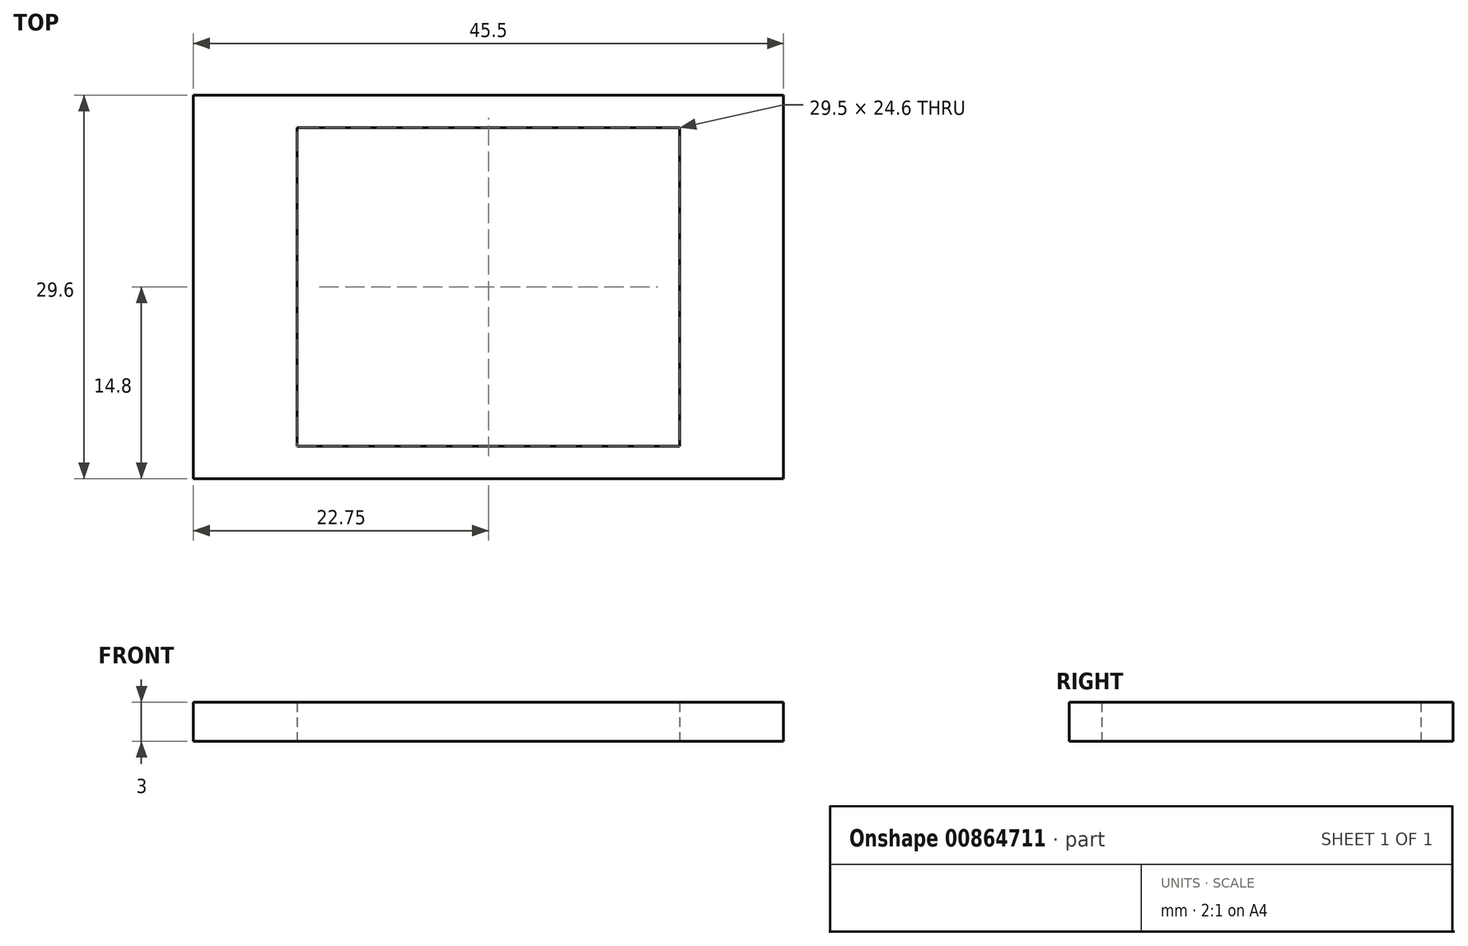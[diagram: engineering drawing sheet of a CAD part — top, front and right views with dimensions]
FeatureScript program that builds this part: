
annotation { "Feature Type Name" : "Feature", "Feature Type Description" : "" }
export const myFeature = defineFeature(function(context is Context, id is Id, definition is map)
    precondition{}
    {
        {
            var Q0;
            Q0=qCreatedBy(makeId("Top.planeOp"),FACE);
            var sketch = newSketch(context, id + "F0", { "sketchPlane" : qUnion([Q0])});
            skLineSegment(sketch, "E0.bottom", {"start": v(0, 0) * mm, "end": v(29.5, 0) * mm});
            skLineSegment(sketch, "E0.top", {"start": v(0, 24.6) * mm, "end": v(29.5, 24.6) * mm});
            skLineSegment(sketch, "E0.left", {"start": v(0, 0) * mm, "end": v(0, 24.6) * mm});
            skLineSegment(sketch, "E0.right", {"start": v(29.5, 0) * mm, "end": v(29.5, 24.6) * mm});
            skLineSegment(sketch, "E1.bottom", {"start": v(-8, 27.1) * mm, "end": v(37.5, 27.1) * mm});
            skLineSegment(sketch, "E1.top", {"start": v(-8, -2.5) * mm, "end": v(37.5, -2.5) * mm});
            skLineSegment(sketch, "E1.left", {"start": v(-8, 27.1) * mm, "end": v(-8, -2.5) * mm});
            skLineSegment(sketch, "E1.right", {"start": v(37.5, 27.1) * mm, "end": v(37.5, -2.5) * mm});
            skSolve(sketch);
        }
        {
            var Q0;
            Q0=makeQuery(id+"F0.imprint","IMPRINT",FACE,{"disambiguationData":[TD([[makeQuery(id+"F0.imprint","IMPRINT",EDGE,{"derivedFrom":sQuery(id+"F0.wireOp",EDGE,"E0.bottom")}),-1.0]])]});
            extrude(context, id + "F1", {"entities" : qUnion([Q0]), "depth" : 3 * mm, "offsetDistance" : 25 * mm});
        }
    });
